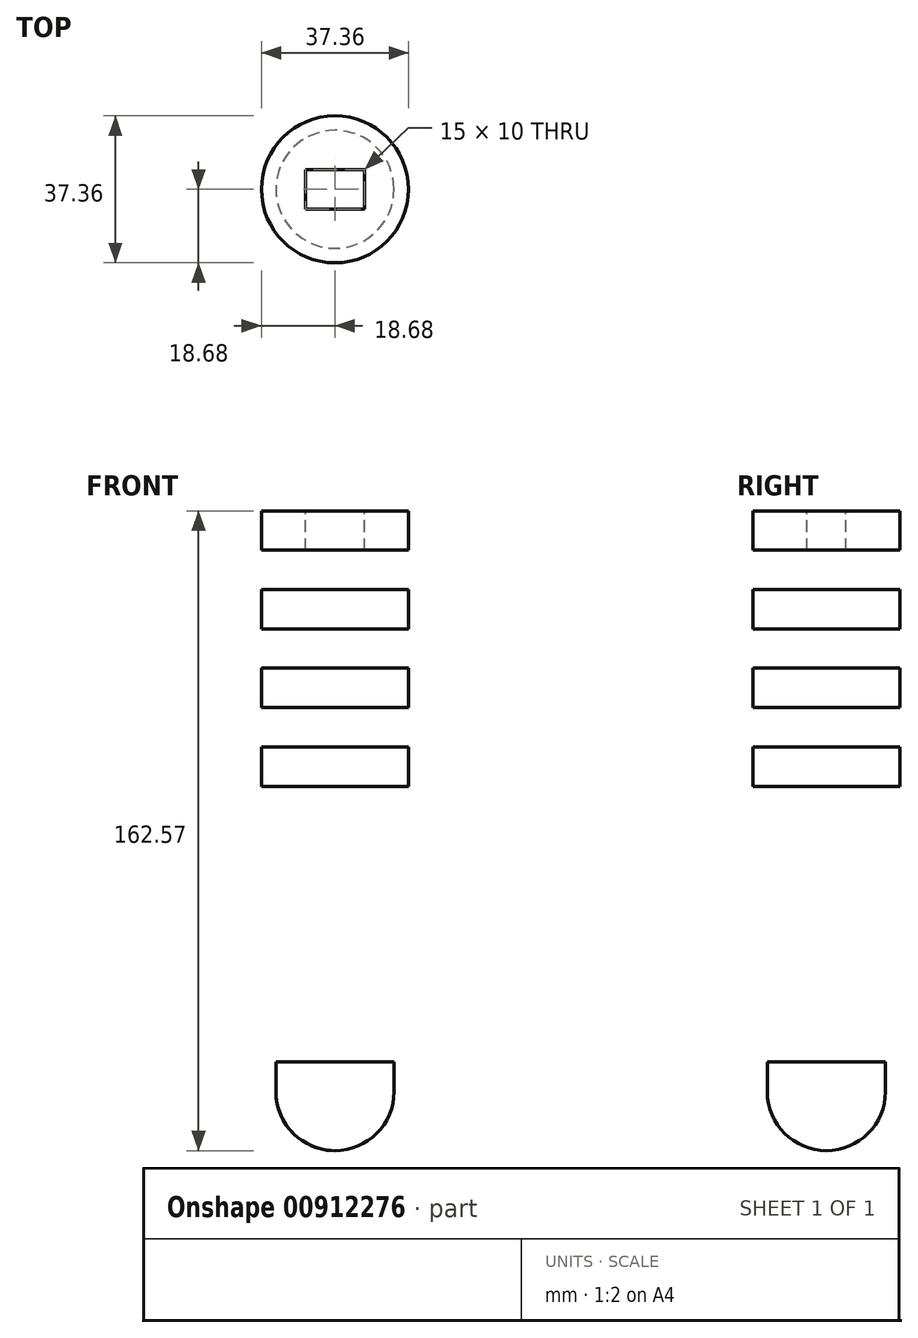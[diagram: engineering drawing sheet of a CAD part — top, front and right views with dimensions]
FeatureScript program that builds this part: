
annotation { "Feature Type Name" : "Feature", "Feature Type Description" : "" }
export const myFeature = defineFeature(function(context is Context, id is Id, definition is map)
    precondition{}
    {
        {
            var Q0;
            Q0=qCreatedBy(makeId("Front.planeOp"),FACE);
            var sketch = newSketch(context, id + "F0", { "sketchPlane" : qUnion([Q0])});
            skLineSegment(sketch, "E0.bottom", {"start": v(0, 0) * mm, "end": v(-18.68, 0) * mm});
            skLineSegment(sketch, "E0.top", {"start": v(0, 10) * mm, "end": v(-18.68, 10) * mm});
            skLineSegment(sketch, "E0.left", {"start": v(0, 0) * mm, "end": v(0, 10) * mm});
            skLineSegment(sketch, "E0.right", {"start": v(-18.68, 0) * mm, "end": v(-18.68, 10) * mm});
            skLineSegment(sketch, "E1.bottom", {"start": v(0, 10) * mm, "end": v(-13.68, 10) * mm});
            skLineSegment(sketch, "E1.top", {"start": v(0, 20) * mm, "end": v(-13.68, 20) * mm});
            skLineSegment(sketch, "E1.left", {"start": v(0, 10) * mm, "end": v(0, 20) * mm});
            skLineSegment(sketch, "E1.right", {"start": v(-13.68, 10) * mm, "end": v(-13.68, 20) * mm});
            skLineSegment(sketch, "E2.bottom", {"start": v(0, 20) * mm, "end": v(-18.68, 20) * mm});
            skLineSegment(sketch, "E2.top", {"start": v(0, 30) * mm, "end": v(-18.68, 30) * mm});
            skLineSegment(sketch, "E2.left", {"start": v(0, 20) * mm, "end": v(0, 30) * mm});
            skLineSegment(sketch, "E2.right", {"start": v(-18.68, 20) * mm, "end": v(-18.68, 30) * mm});
            skLineSegment(sketch, "E3.bottom", {"start": v(0, 30) * mm, "end": v(-13.68, 30) * mm});
            skLineSegment(sketch, "E3.top", {"start": v(0, 40) * mm, "end": v(-13.68, 40) * mm});
            skLineSegment(sketch, "E3.left", {"start": v(0, 30) * mm, "end": v(0, 40) * mm});
            skLineSegment(sketch, "E3.right", {"start": v(-13.68, 30) * mm, "end": v(-13.68, 40) * mm});
            skLineSegment(sketch, "E4.bottom", {"start": v(0, 40) * mm, "end": v(-18.68, 40) * mm});
            skLineSegment(sketch, "E4.top", {"start": v(0, 50) * mm, "end": v(-18.68, 50) * mm});
            skLineSegment(sketch, "E4.left", {"start": v(0, 40) * mm, "end": v(0, 50) * mm});
            skLineSegment(sketch, "E4.right", {"start": v(-18.68, 40) * mm, "end": v(-18.68, 50) * mm});
            skLineSegment(sketch, "E5.bottom", {"start": v(0, 50) * mm, "end": v(-13.68, 50) * mm});
            skLineSegment(sketch, "E5.top", {"start": v(0, 60) * mm, "end": v(-13.68, 60) * mm});
            skLineSegment(sketch, "E5.left", {"start": v(0, 50) * mm, "end": v(0, 60) * mm});
            skLineSegment(sketch, "E5.right", {"start": v(-13.68, 50) * mm, "end": v(-13.68, 60) * mm});
            skLineSegment(sketch, "E6.bottom", {"start": v(0, 60) * mm, "end": v(-18.68, 60) * mm});
            skLineSegment(sketch, "E6.top", {"start": v(0, 70) * mm, "end": v(-18.68, 70) * mm});
            skLineSegment(sketch, "E6.left", {"start": v(0, 60) * mm, "end": v(0, 70) * mm});
            skLineSegment(sketch, "E6.right", {"start": v(-18.68, 60) * mm, "end": v(-18.68, 70) * mm});
            skLineSegment(sketch, "E7.bottom", {"start": v(0, 0) * mm, "end": v(-13.68, 0) * mm});
            skLineSegment(sketch, "E7.top", {"start": v(0, -70) * mm, "end": v(-13.68, -70) * mm});
            skLineSegment(sketch, "E7.left", {"start": v(0, 0) * mm, "end": v(0, -70) * mm});
            skLineSegment(sketch, "E7.right", {"start": v(-13.68, 0) * mm, "end": v(-13.68, -70) * mm});
            skLineSegment(sketch, "E8.bottom", {"start": v(0, -77.57) * mm, "end": v(-15, -77.57) * mm});
            skLineSegment(sketch, "E8.top", {"start": v(0, -70) * mm, "end": v(-15, -70) * mm});
            skLineSegment(sketch, "E8.left", {"start": v(0, -77.57) * mm, "end": v(0, -70) * mm});
            skLineSegment(sketch, "E8.right", {"start": v(-15, -77.57) * mm, "end": v(-15, -70) * mm});
            skLineSegment(sketch, "E9", {"start": v(0, -77.57) * mm, "end": v(0, -92.57) * mm});
            skArc(sketch, "E10", {"start": v(0, -92.57) * mm, "mid": v(-10.6, -88.18) * mm, "end": v(-15, -77.57) * mm});
            skSolve(sketch);
        }
        {
            var Q0;
            Q0=makeQuery(id+"F0.imprint","IMPRINT",FACE,{"disambiguationData":[TD([[makeQuery(id+"F0.imprint","IMPRINT",EDGE,{"derivedFrom":sQuery(id+"F0.wireOp",EDGE,"E6.top")}),1.0]])]});
            var Q1;
            Q1=makeQuery(id+"F0.imprint","IMPRINT",FACE,{"disambiguationData":[TD([[makeQuery(id+"F0.imprint","IMPRINT",EDGE,{"derivedFrom":sQuery(id+"F0.wireOp",EDGE,"E5.bottom")}),-1.0]])]});
            var Q2;
            Q2=makeQuery(id+"F0.imprint","IMPRINT",FACE,{"disambiguationData":[TD([[makeQuery(id+"F0.imprint","IMPRINT",EDGE,{"derivedFrom":sQuery(id+"F0.wireOp",EDGE,"E4.top")}),1.0]])]});
            var Q3;
            Q3=makeQuery(id+"F0.imprint","IMPRINT",FACE,{"disambiguationData":[TD([[makeQuery(id+"F0.imprint","IMPRINT",EDGE,{"derivedFrom":sQuery(id+"F0.wireOp",EDGE,"E3.bottom")}),-1.0]])]});
            var Q4;
            Q4=makeQuery(id+"F0.imprint","IMPRINT",FACE,{"disambiguationData":[TD([[makeQuery(id+"F0.imprint","IMPRINT",EDGE,{"derivedFrom":sQuery(id+"F0.wireOp",EDGE,"E2.top")}),1.0]])]});
            var Q5;
            Q5=makeQuery(id+"F0.imprint","IMPRINT",FACE,{"disambiguationData":[TD([[makeQuery(id+"F0.imprint","IMPRINT",EDGE,{"derivedFrom":sQuery(id+"F0.wireOp",EDGE,"E1.bottom")}),-1.0]])]});
            var Q6;
            Q6=makeQuery(id+"F0.imprint","IMPRINT",FACE,{"disambiguationData":[TD([[makeQuery(id+"F0.imprint","IMPRINT",EDGE,{"derivedFrom":sQuery(id+"F0.wireOp",EDGE,"E0.bottom")}),-1.0]])]});
            var Q7;
            Q7=makeQuery(id+"F0.imprint","IMPRINT",FACE,{"disambiguationData":[TD([[makeQuery(id+"F0.imprint","IMPRINT",EDGE,{"derivedFrom":sQuery(id+"F0.wireOp",EDGE,"E7.bottom")}),1.0]])]});
            var Q8;
            Q8=makeQuery(id+"F0.imprint","IMPRINT",FACE,{"disambiguationData":[TD([[makeQuery(id+"F0.imprint","IMPRINT",EDGE,{"derivedFrom":sQuery(id+"F0.wireOp",EDGE,"E8.bottom")}),-1.0]])]});
            var Q9;
            Q9=makeQuery(id+"F0.imprint","IMPRINT",FACE,{"disambiguationData":[TD([[makeQuery(id+"F0.imprint","IMPRINT",EDGE,{"derivedFrom":sQuery(id+"F0.wireOp",EDGE,"E8.bottom")}),1.0]])]});
            var Q10;
            Q10=sQuery(id+"F0.wireOp",EDGE,"E3.left");
            revolve(context, id + "F1", {"surfaceOperationType" : NewSurfaceOperationType.NEW, "entities" : qUnion([Q0, Q1, Q2, Q3, Q4, Q5, Q6, Q7, Q8, Q9]), "axis" : qUnion([Q10]), "revolveType" : RevolveType.FULL});
        }
        {
            var Q0;
            Q0=makeQuery(id+"F1.opRevolve","SWEPT_FACE",FACE,{"disambiguationData":[OSD([sQuery(id+"F0.wireOp",EDGE,"E6.top")])]});
            var sketch = newSketch(context, id + "F2", { "sketchPlane" : qUnion([Q0])});
            skLineSegment(sketch, "E11.bottom", {"start": v(-7.5, 5) * mm, "end": v(7.5, 5) * mm});
            skLineSegment(sketch, "E11.top", {"start": v(-7.5, -5) * mm, "end": v(7.5, -5) * mm});
            skLineSegment(sketch, "E11.left", {"start": v(-7.5, 5) * mm, "end": v(-7.5, -5) * mm});
            skLineSegment(sketch, "E11.right", {"start": v(7.5, 5) * mm, "end": v(7.5, -5) * mm});
            skPoint(sketch, "E11.middle", {"position": v(0, 0) * mm});
            skSolve(sketch);
        }
        {
            var Q0;
            Q0=makeQuery(id+"F2.imprint","IMPRINT",FACE,{"disambiguationData":[TD([[makeQuery(id+"F2.imprint","IMPRINT",EDGE,{"derivedFrom":sQuery(id+"F2.wireOp",EDGE,"E11.bottom")}),-1.0]])]});
            extrude(context, id + "F3", {"entities" : qUnion([Q0]), "operationType" : NewBodyOperationType.REMOVE, "oppositeDirection" : true, "depth" : 15 * mm, "offsetDistance" : 25 * mm});
        }
    });
